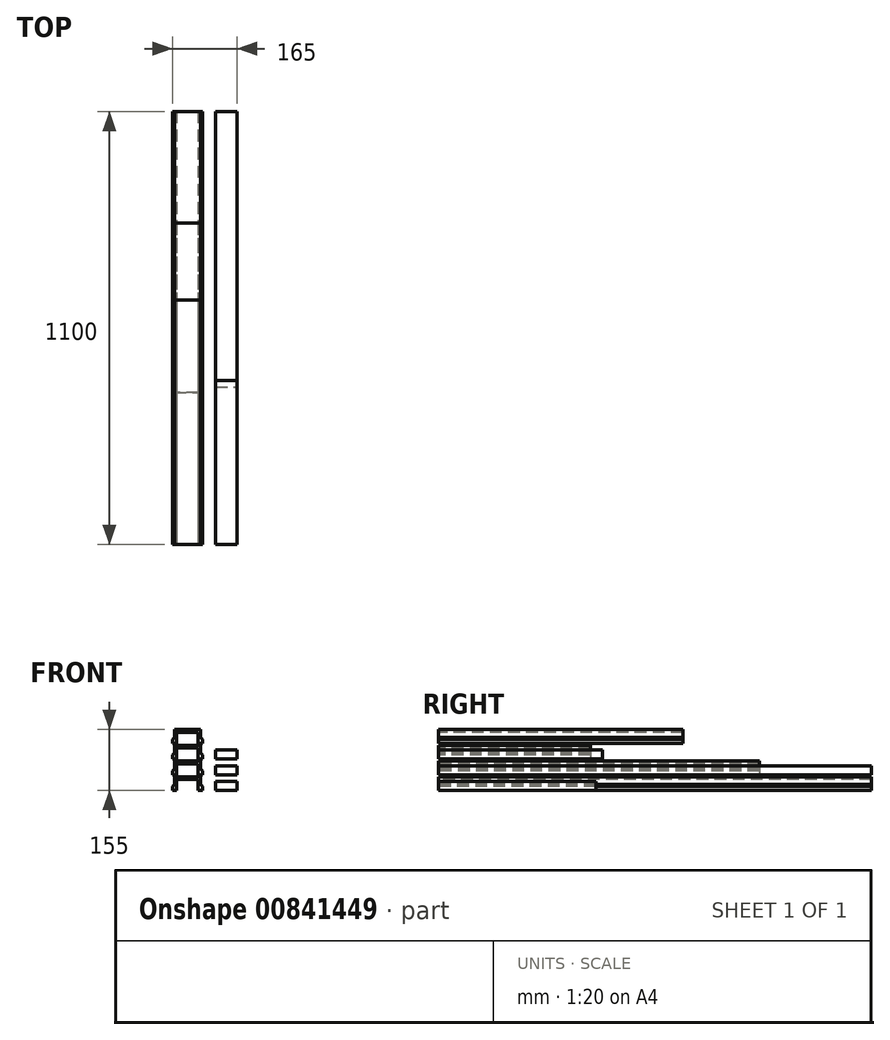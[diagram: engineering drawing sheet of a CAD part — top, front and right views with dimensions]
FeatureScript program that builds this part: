
annotation { "Feature Type Name" : "Feature", "Feature Type Description" : "" }
export const myFeature = defineFeature(function(context is Context, id is Id, definition is map)
    precondition{}
    {
        {
            var Q0;
            Q0=qCreatedBy(makeId("Front.planeOp"),FACE);
            var sketch = newSketch(context, id + "F0", { "sketchPlane" : qUnion([Q0])});
            skLineSegment(sketch, "E0", {"start": v(0, 0) * mm, "end": v(0, 10) * mm});
            skLineSegment(sketch, "E1", {"start": v(0, 10) * mm, "end": v(5.5, 15) * mm});
            skLineSegment(sketch, "E2", {"start": v(5.5, 15) * mm, "end": v(5.5, 35) * mm});
            skLineSegment(sketch, "E3", {"start": v(5.5, 35) * mm, "end": v(71.5, 35) * mm});
            skLineSegment(sketch, "E4", {"start": v(71.5, 35) * mm, "end": v(71.5, 15) * mm});
            skLineSegment(sketch, "E5", {"start": v(71.5, 15) * mm, "end": v(77, 10) * mm});
            skLineSegment(sketch, "E6", {"start": v(77, 10) * mm, "end": v(77, 0) * mm});
            skLineSegment(sketch, "E7", {"start": v(77, 0) * mm, "end": v(66, 0) * mm});
            skLineSegment(sketch, "E8", {"start": v(66, 0) * mm, "end": v(66, 28) * mm});
            skLineSegment(sketch, "E9", {"start": v(66, 28) * mm, "end": v(11, 28) * mm});
            skLineSegment(sketch, "E10", {"start": v(11, 28) * mm, "end": v(11, 0) * mm});
            skLineSegment(sketch, "E11", {"start": v(11, 0) * mm, "end": v(0, 0) * mm});
            skLineSegment(sketch, "E12.0.1.0", {"start": v(0, 40) * mm, "end": v(0, 50) * mm});
            skLineSegment(sketch, "E12.0.1.1", {"start": v(0, 50) * mm, "end": v(5.5, 55) * mm});
            skLineSegment(sketch, "E12.0.1.2", {"start": v(5.5, 55) * mm, "end": v(5.5, 75) * mm});
            skLineSegment(sketch, "E12.0.1.3", {"start": v(5.5, 75) * mm, "end": v(71.5, 75) * mm});
            skLineSegment(sketch, "E12.0.1.5", {"start": v(66, 68) * mm, "end": v(11, 68) * mm});
            skLineSegment(sketch, "E12.0.1.6", {"start": v(11, 68) * mm, "end": v(11, 40) * mm});
            skLineSegment(sketch, "E12.0.1.8", {"start": v(11, 40) * mm, "end": v(0, 40) * mm});
            skLineSegment(sketch, "E12.0.1.11", {"start": v(71.5, 75) * mm, "end": v(71.5, 55) * mm});
            skLineSegment(sketch, "E12.0.1.12", {"start": v(66, 40) * mm, "end": v(66, 68) * mm});
            skLineSegment(sketch, "E12.0.1.13", {"start": v(71.5, 55) * mm, "end": v(77, 50) * mm});
            skLineSegment(sketch, "E12.0.1.14", {"start": v(77, 50) * mm, "end": v(77, 40) * mm});
            skLineSegment(sketch, "E12.0.1.15", {"start": v(77, 40) * mm, "end": v(66, 40) * mm});
            skLineSegment(sketch, "E12.0.2.0", {"start": v(0, 80) * mm, "end": v(0, 90) * mm});
            skLineSegment(sketch, "E12.0.2.1", {"start": v(0, 90) * mm, "end": v(5.5, 95) * mm});
            skLineSegment(sketch, "E12.0.2.2", {"start": v(5.5, 95) * mm, "end": v(5.5, 115) * mm});
            skLineSegment(sketch, "E12.0.2.3", {"start": v(5.5, 115) * mm, "end": v(71.5, 115) * mm});
            skLineSegment(sketch, "E12.0.2.5", {"start": v(66, 108) * mm, "end": v(11, 108) * mm});
            skLineSegment(sketch, "E12.0.2.6", {"start": v(11, 108) * mm, "end": v(11, 80) * mm});
            skLineSegment(sketch, "E12.0.2.8", {"start": v(11, 80) * mm, "end": v(0, 80) * mm});
            skLineSegment(sketch, "E12.0.2.11", {"start": v(71.5, 115) * mm, "end": v(71.5, 95) * mm});
            skLineSegment(sketch, "E12.0.2.12", {"start": v(66, 80) * mm, "end": v(66, 108) * mm});
            skLineSegment(sketch, "E12.0.2.13", {"start": v(71.5, 95) * mm, "end": v(77, 90) * mm});
            skLineSegment(sketch, "E12.0.2.14", {"start": v(77, 90) * mm, "end": v(77, 80) * mm});
            skLineSegment(sketch, "E12.0.2.15", {"start": v(77, 80) * mm, "end": v(66, 80) * mm});
            skLineSegment(sketch, "E12.0.3.0", {"start": v(0, 120) * mm, "end": v(0, 130) * mm});
            skLineSegment(sketch, "E12.0.3.1", {"start": v(0, 130) * mm, "end": v(5.5, 135) * mm});
            skLineSegment(sketch, "E12.0.3.2", {"start": v(5.5, 135) * mm, "end": v(5.5, 155) * mm});
            skLineSegment(sketch, "E12.0.3.3", {"start": v(5.5, 155) * mm, "end": v(71.5, 155) * mm});
            skLineSegment(sketch, "E12.0.3.5", {"start": v(66, 148) * mm, "end": v(11, 148) * mm});
            skLineSegment(sketch, "E12.0.3.6", {"start": v(11, 148) * mm, "end": v(11, 120) * mm});
            skLineSegment(sketch, "E12.0.3.8", {"start": v(11, 120) * mm, "end": v(0, 120) * mm});
            skLineSegment(sketch, "E12.0.3.11", {"start": v(71.5, 155) * mm, "end": v(71.5, 135) * mm});
            skLineSegment(sketch, "E12.0.3.12", {"start": v(66, 120) * mm, "end": v(66, 148) * mm});
            skLineSegment(sketch, "E12.0.3.13", {"start": v(71.5, 135) * mm, "end": v(77, 130) * mm});
            skLineSegment(sketch, "E12.0.3.14", {"start": v(77, 130) * mm, "end": v(77, 120) * mm});
            skLineSegment(sketch, "E12.0.3.15", {"start": v(77, 120) * mm, "end": v(66, 120) * mm});
            skLineSegment(sketch, "E12.0.4.0", {"start": v(0, 160) * mm, "end": v(0, 170) * mm});
            skLineSegment(sketch, "E12.0.4.1", {"start": v(0, 170) * mm, "end": v(5.5, 175) * mm});
            skLineSegment(sketch, "E12.0.4.2", {"start": v(5.5, 175) * mm, "end": v(5.5, 195) * mm});
            skLineSegment(sketch, "E12.0.4.3", {"start": v(5.5, 195) * mm, "end": v(71.5, 195) * mm});
            skLineSegment(sketch, "E12.0.4.5", {"start": v(66, 188) * mm, "end": v(11, 188) * mm});
            skLineSegment(sketch, "E12.0.4.6", {"start": v(11, 188) * mm, "end": v(11, 160) * mm});
            skLineSegment(sketch, "E12.0.4.8", {"start": v(11, 160) * mm, "end": v(0, 160) * mm});
            skLineSegment(sketch, "E12.0.4.11", {"start": v(71.5, 195) * mm, "end": v(71.5, 175) * mm});
            skLineSegment(sketch, "E12.0.4.12", {"start": v(66, 160) * mm, "end": v(66, 188) * mm});
            skLineSegment(sketch, "E12.0.4.13", {"start": v(71.5, 175) * mm, "end": v(77, 170) * mm});
            skLineSegment(sketch, "E12.0.4.14", {"start": v(77, 170) * mm, "end": v(77, 160) * mm});
            skLineSegment(sketch, "E12.0.4.15", {"start": v(77, 160) * mm, "end": v(66, 160) * mm});
            skLineSegment(sketch, "E12.0.5.0", {"start": v(0, 200) * mm, "end": v(0, 210) * mm});
            skLineSegment(sketch, "E12.0.5.1", {"start": v(0, 210) * mm, "end": v(5.5, 215) * mm});
            skLineSegment(sketch, "E12.0.5.2", {"start": v(5.5, 215) * mm, "end": v(5.5, 235) * mm});
            skLineSegment(sketch, "E12.0.5.3", {"start": v(5.5, 235) * mm, "end": v(71.5, 235) * mm});
            skLineSegment(sketch, "E12.0.5.5", {"start": v(66, 228) * mm, "end": v(11, 228) * mm});
            skLineSegment(sketch, "E12.0.5.6", {"start": v(11, 228) * mm, "end": v(11, 200) * mm});
            skLineSegment(sketch, "E12.0.5.8", {"start": v(11, 200) * mm, "end": v(0, 200) * mm});
            skLineSegment(sketch, "E12.0.5.11", {"start": v(71.5, 235) * mm, "end": v(71.5, 215) * mm});
            skLineSegment(sketch, "E12.0.5.12", {"start": v(66, 200) * mm, "end": v(66, 228) * mm});
            skLineSegment(sketch, "E12.0.5.13", {"start": v(71.5, 215) * mm, "end": v(77, 210) * mm});
            skLineSegment(sketch, "E12.0.5.14", {"start": v(77, 210) * mm, "end": v(77, 200) * mm});
            skLineSegment(sketch, "E12.0.5.15", {"start": v(77, 200) * mm, "end": v(66, 200) * mm});
            skLineSegment(sketch, "E12.0.6.0", {"start": v(0, 240) * mm, "end": v(0, 250) * mm});
            skLineSegment(sketch, "E12.0.6.1", {"start": v(0, 250) * mm, "end": v(5.5, 255) * mm});
            skLineSegment(sketch, "E12.0.6.2", {"start": v(5.5, 255) * mm, "end": v(5.5, 275) * mm});
            skLineSegment(sketch, "E12.0.6.3", {"start": v(5.5, 275) * mm, "end": v(71.5, 275) * mm});
            skLineSegment(sketch, "E12.0.6.5", {"start": v(66, 268) * mm, "end": v(11, 268) * mm});
            skLineSegment(sketch, "E12.0.6.6", {"start": v(11, 268) * mm, "end": v(11, 240) * mm});
            skLineSegment(sketch, "E12.0.6.8", {"start": v(11, 240) * mm, "end": v(0, 240) * mm});
            skLineSegment(sketch, "E12.0.6.11", {"start": v(71.5, 275) * mm, "end": v(71.5, 255) * mm});
            skLineSegment(sketch, "E12.0.6.12", {"start": v(66, 240) * mm, "end": v(66, 268) * mm});
            skLineSegment(sketch, "E12.0.6.13", {"start": v(71.5, 255) * mm, "end": v(77, 250) * mm});
            skLineSegment(sketch, "E12.0.6.14", {"start": v(77, 250) * mm, "end": v(77, 240) * mm});
            skLineSegment(sketch, "E12.0.6.15", {"start": v(77, 240) * mm, "end": v(66, 240) * mm});
            skLineSegment(sketch, "E12.0.7.0", {"start": v(0, 280) * mm, "end": v(0, 290) * mm});
            skLineSegment(sketch, "E12.0.7.1", {"start": v(0, 290) * mm, "end": v(5.5, 295) * mm});
            skLineSegment(sketch, "E12.0.7.2", {"start": v(5.5, 295) * mm, "end": v(5.5, 315) * mm});
            skLineSegment(sketch, "E12.0.7.3", {"start": v(5.5, 315) * mm, "end": v(71.5, 315) * mm});
            skLineSegment(sketch, "E12.0.7.5", {"start": v(66, 308) * mm, "end": v(11, 308) * mm});
            skLineSegment(sketch, "E12.0.7.6", {"start": v(11, 308) * mm, "end": v(11, 280) * mm});
            skLineSegment(sketch, "E12.0.7.8", {"start": v(11, 280) * mm, "end": v(0, 280) * mm});
            skLineSegment(sketch, "E12.0.7.11", {"start": v(71.5, 315) * mm, "end": v(71.5, 295) * mm});
            skLineSegment(sketch, "E12.0.7.12", {"start": v(66, 280) * mm, "end": v(66, 308) * mm});
            skLineSegment(sketch, "E12.0.7.13", {"start": v(71.5, 295) * mm, "end": v(77, 290) * mm});
            skLineSegment(sketch, "E12.0.7.14", {"start": v(77, 290) * mm, "end": v(77, 280) * mm});
            skLineSegment(sketch, "E12.0.7.15", {"start": v(77, 280) * mm, "end": v(66, 280) * mm});
            skLineSegment(sketch, "E12.0.8.0", {"start": v(0, 320) * mm, "end": v(0, 330) * mm});
            skLineSegment(sketch, "E12.0.8.1", {"start": v(0, 330) * mm, "end": v(5.5, 335) * mm});
            skLineSegment(sketch, "E12.0.8.2", {"start": v(5.5, 335) * mm, "end": v(5.5, 355) * mm});
            skLineSegment(sketch, "E12.0.8.3", {"start": v(5.5, 355) * mm, "end": v(71.5, 355) * mm});
            skLineSegment(sketch, "E12.0.8.5", {"start": v(66, 348) * mm, "end": v(11, 348) * mm});
            skLineSegment(sketch, "E12.0.8.6", {"start": v(11, 348) * mm, "end": v(11, 320) * mm});
            skLineSegment(sketch, "E12.0.8.8", {"start": v(11, 320) * mm, "end": v(0, 320) * mm});
            skLineSegment(sketch, "E12.0.8.11", {"start": v(71.5, 355) * mm, "end": v(71.5, 335) * mm});
            skLineSegment(sketch, "E12.0.8.12", {"start": v(66, 320) * mm, "end": v(66, 348) * mm});
            skLineSegment(sketch, "E12.0.8.13", {"start": v(71.5, 335) * mm, "end": v(77, 330) * mm});
            skLineSegment(sketch, "E12.0.8.14", {"start": v(77, 330) * mm, "end": v(77, 320) * mm});
            skLineSegment(sketch, "E12.0.8.15", {"start": v(77, 320) * mm, "end": v(66, 320) * mm});
            skLineSegment(sketch, "E12.0.9.0", {"start": v(0, 360) * mm, "end": v(0, 370) * mm});
            skLineSegment(sketch, "E12.0.9.1", {"start": v(0, 370) * mm, "end": v(5.5, 375) * mm});
            skLineSegment(sketch, "E12.0.9.2", {"start": v(5.5, 375) * mm, "end": v(5.5, 395) * mm});
            skLineSegment(sketch, "E12.0.9.3", {"start": v(5.5, 395) * mm, "end": v(71.5, 395) * mm});
            skLineSegment(sketch, "E12.0.9.5", {"start": v(66, 388) * mm, "end": v(11, 388) * mm});
            skLineSegment(sketch, "E12.0.9.6", {"start": v(11, 388) * mm, "end": v(11, 360) * mm});
            skLineSegment(sketch, "E12.0.9.8", {"start": v(11, 360) * mm, "end": v(0, 360) * mm});
            skLineSegment(sketch, "E12.0.9.11", {"start": v(71.5, 395) * mm, "end": v(71.5, 375) * mm});
            skLineSegment(sketch, "E12.0.9.12", {"start": v(66, 360) * mm, "end": v(66, 388) * mm});
            skLineSegment(sketch, "E12.0.9.13", {"start": v(71.5, 375) * mm, "end": v(77, 370) * mm});
            skLineSegment(sketch, "E12.0.9.14", {"start": v(77, 370) * mm, "end": v(77, 360) * mm});
            skLineSegment(sketch, "E12.0.9.15", {"start": v(77, 360) * mm, "end": v(66, 360) * mm});
            skLineSegment(sketch, "E12.direction1", {"start": v(0, 0) * mm, "end": v(25, 0) * mm, "construction": true});
            skLineSegment(sketch, "E12.direction2", {"start": v(0, 0) * mm, "end": v(0, 40) * mm, "construction": true});
            skSolve(sketch);
        }
        {
            var Q0;
            Q0=makeQuery(id+"F0.imprint","IMPRINT",FACE,{"disambiguationData":[TD([[makeQuery(id+"F0.imprint","IMPRINT",EDGE,{"derivedFrom":sQuery(id+"F0.wireOp",EDGE,"E0")}),-1.0]])]});
            extrude(context, id + "F1", {"entities" : qUnion([Q0]), "oppositeDirection" : true, "depth" : 1100 * mm, "offsetDistance" : 25 * mm});
        }
        {
            var Q0;
            Q0=makeQuery(id+"F0.imprint","IMPRINT",FACE,{"disambiguationData":[TD([[makeQuery(id+"F0.imprint","IMPRINT",EDGE,{"derivedFrom":sQuery(id+"F0.wireOp",EDGE,"E12.0.1.0")}),-1.0]])]});
            extrude(context, id + "F2", {"entities" : qUnion([Q0]), "oppositeDirection" : true, "depth" : 816 * mm, "offsetDistance" : 25 * mm});
        }
        {
            var Q0;
            Q0=makeQuery(id+"F0.imprint","IMPRINT",FACE,{"disambiguationData":[TD([[makeQuery(id+"F0.imprint","IMPRINT",EDGE,{"derivedFrom":sQuery(id+"F0.wireOp",EDGE,"E12.0.2.0")}),-1.0]])]});
            extrude(context, id + "F3", {"entities" : qUnion([Q0]), "oppositeDirection" : true, "depth" : 386 * mm, "offsetDistance" : 25 * mm});
        }
        {
            var Q0;
            Q0=makeQuery(id+"F0.imprint","IMPRINT",FACE,{"disambiguationData":[TD([[makeQuery(id+"F0.imprint","IMPRINT",EDGE,{"derivedFrom":sQuery(id+"F0.wireOp",EDGE,"E12.0.3.0")}),-1.0]])]});
            extrude(context, id + "F4", {"entities" : qUnion([Q0]), "oppositeDirection" : true, "depth" : 621 * mm, "offsetDistance" : 25 * mm});
        }
        {
            var Q0;
            Q0=qCreatedBy(makeId("Front.planeOp"),FACE);
            var sketch = newSketch(context, id + "F5", { "sketchPlane" : qUnion([Q0])});
            skLineSegment(sketch, "E13.bottom", {"start": v(110, 0) * mm, "end": v(165, 0) * mm});
            skLineSegment(sketch, "E13.top", {"start": v(110, 23) * mm, "end": v(165, 23) * mm});
            skLineSegment(sketch, "E13.left", {"start": v(110, 0) * mm, "end": v(110, 23) * mm});
            skLineSegment(sketch, "E13.right", {"start": v(165, 0) * mm, "end": v(165, 23) * mm});
            skLineSegment(sketch, "E14.0.1.0", {"start": v(110, 40) * mm, "end": v(110, 63) * mm});
            skLineSegment(sketch, "E14.0.1.1", {"start": v(110, 63) * mm, "end": v(165, 63) * mm});
            skLineSegment(sketch, "E14.0.1.2", {"start": v(165, 40) * mm, "end": v(165, 63) * mm});
            skLineSegment(sketch, "E14.0.1.3", {"start": v(110, 40) * mm, "end": v(165, 40) * mm});
            skLineSegment(sketch, "E14.0.2.0", {"start": v(110, 80) * mm, "end": v(110, 103) * mm});
            skLineSegment(sketch, "E14.0.2.1", {"start": v(110, 103) * mm, "end": v(165, 103) * mm});
            skLineSegment(sketch, "E14.0.2.2", {"start": v(165, 80) * mm, "end": v(165, 103) * mm});
            skLineSegment(sketch, "E14.0.2.3", {"start": v(110, 80) * mm, "end": v(165, 80) * mm});
            skLineSegment(sketch, "E14.0.3.0", {"start": v(110, 120) * mm, "end": v(110, 143) * mm});
            skLineSegment(sketch, "E14.0.3.1", {"start": v(110, 143) * mm, "end": v(165, 143) * mm});
            skLineSegment(sketch, "E14.0.3.2", {"start": v(165, 120) * mm, "end": v(165, 143) * mm});
            skLineSegment(sketch, "E14.0.3.3", {"start": v(110, 120) * mm, "end": v(165, 120) * mm});
            skLineSegment(sketch, "E14.0.4.0", {"start": v(110, 160) * mm, "end": v(110, 183) * mm});
            skLineSegment(sketch, "E14.0.4.1", {"start": v(110, 183) * mm, "end": v(165, 183) * mm});
            skLineSegment(sketch, "E14.0.4.2", {"start": v(165, 160) * mm, "end": v(165, 183) * mm});
            skLineSegment(sketch, "E14.0.4.3", {"start": v(110, 160) * mm, "end": v(165, 160) * mm});
            skLineSegment(sketch, "E14.0.5.0", {"start": v(110, 200) * mm, "end": v(110, 223) * mm});
            skLineSegment(sketch, "E14.0.5.1", {"start": v(110, 223) * mm, "end": v(165, 223) * mm});
            skLineSegment(sketch, "E14.0.5.2", {"start": v(165, 200) * mm, "end": v(165, 223) * mm});
            skLineSegment(sketch, "E14.0.5.3", {"start": v(110, 200) * mm, "end": v(165, 200) * mm});
            skLineSegment(sketch, "E14.0.6.0", {"start": v(110, 240) * mm, "end": v(110, 263) * mm});
            skLineSegment(sketch, "E14.0.6.1", {"start": v(110, 263) * mm, "end": v(165, 263) * mm});
            skLineSegment(sketch, "E14.0.6.2", {"start": v(165, 240) * mm, "end": v(165, 263) * mm});
            skLineSegment(sketch, "E14.0.6.3", {"start": v(110, 240) * mm, "end": v(165, 240) * mm});
            skLineSegment(sketch, "E14.0.7.0", {"start": v(110, 280) * mm, "end": v(110, 303) * mm});
            skLineSegment(sketch, "E14.0.7.1", {"start": v(110, 303) * mm, "end": v(165, 303) * mm});
            skLineSegment(sketch, "E14.0.7.2", {"start": v(165, 280) * mm, "end": v(165, 303) * mm});
            skLineSegment(sketch, "E14.0.7.3", {"start": v(110, 280) * mm, "end": v(165, 280) * mm});
            skLineSegment(sketch, "E14.0.8.0", {"start": v(110, 320) * mm, "end": v(110, 343) * mm});
            skLineSegment(sketch, "E14.0.8.1", {"start": v(110, 343) * mm, "end": v(165, 343) * mm});
            skLineSegment(sketch, "E14.0.8.2", {"start": v(165, 320) * mm, "end": v(165, 343) * mm});
            skLineSegment(sketch, "E14.0.8.3", {"start": v(110, 320) * mm, "end": v(165, 320) * mm});
            skLineSegment(sketch, "E14.0.9.0", {"start": v(110, 360) * mm, "end": v(110, 383) * mm});
            skLineSegment(sketch, "E14.0.9.1", {"start": v(110, 383) * mm, "end": v(165, 383) * mm});
            skLineSegment(sketch, "E14.0.9.2", {"start": v(165, 360) * mm, "end": v(165, 383) * mm});
            skLineSegment(sketch, "E14.0.9.3", {"start": v(110, 360) * mm, "end": v(165, 360) * mm});
            skLineSegment(sketch, "E14.direction1", {"start": v(110, 0) * mm, "end": v(135, 0) * mm, "construction": true});
            skLineSegment(sketch, "E14.direction2", {"start": v(110, 0) * mm, "end": v(110, 40) * mm, "construction": true});
            skSolve(sketch);
        }
        {
            var Q0;
            Q0=makeQuery(id+"F5.imprint","IMPRINT",FACE,{"disambiguationData":[TD([[makeQuery(id+"F5.imprint","IMPRINT",EDGE,{"derivedFrom":sQuery(id+"F5.wireOp",EDGE,"E13.bottom")}),1.0]])]});
            extrude(context, id + "F6", {"entities" : qUnion([Q0]), "oppositeDirection" : true, "depth" : 400 * mm, "offsetDistance" : 25 * mm});
        }
        {
            var Q0;
            Q0=makeQuery(id+"F5.imprint","IMPRINT",FACE,{"disambiguationData":[TD([[makeQuery(id+"F5.imprint","IMPRINT",EDGE,{"derivedFrom":sQuery(id+"F5.wireOp",EDGE,"E14.0.1.0")}),-1.0]])]});
            extrude(context, id + "F7", {"entities" : qUnion([Q0]), "oppositeDirection" : true, "depth" : 1100 * mm, "offsetDistance" : 25 * mm});
        }
        {
            var Q0;
            Q0=makeQuery(id+"F5.imprint","IMPRINT",FACE,{"disambiguationData":[TD([[makeQuery(id+"F5.imprint","IMPRINT",EDGE,{"derivedFrom":sQuery(id+"F5.wireOp",EDGE,"E14.0.2.0")}),-1.0]])]});
            extrude(context, id + "F8", {"entities" : qUnion([Q0]), "oppositeDirection" : true, "depth" : 417 * mm, "offsetDistance" : 25 * mm});
        }
    });
